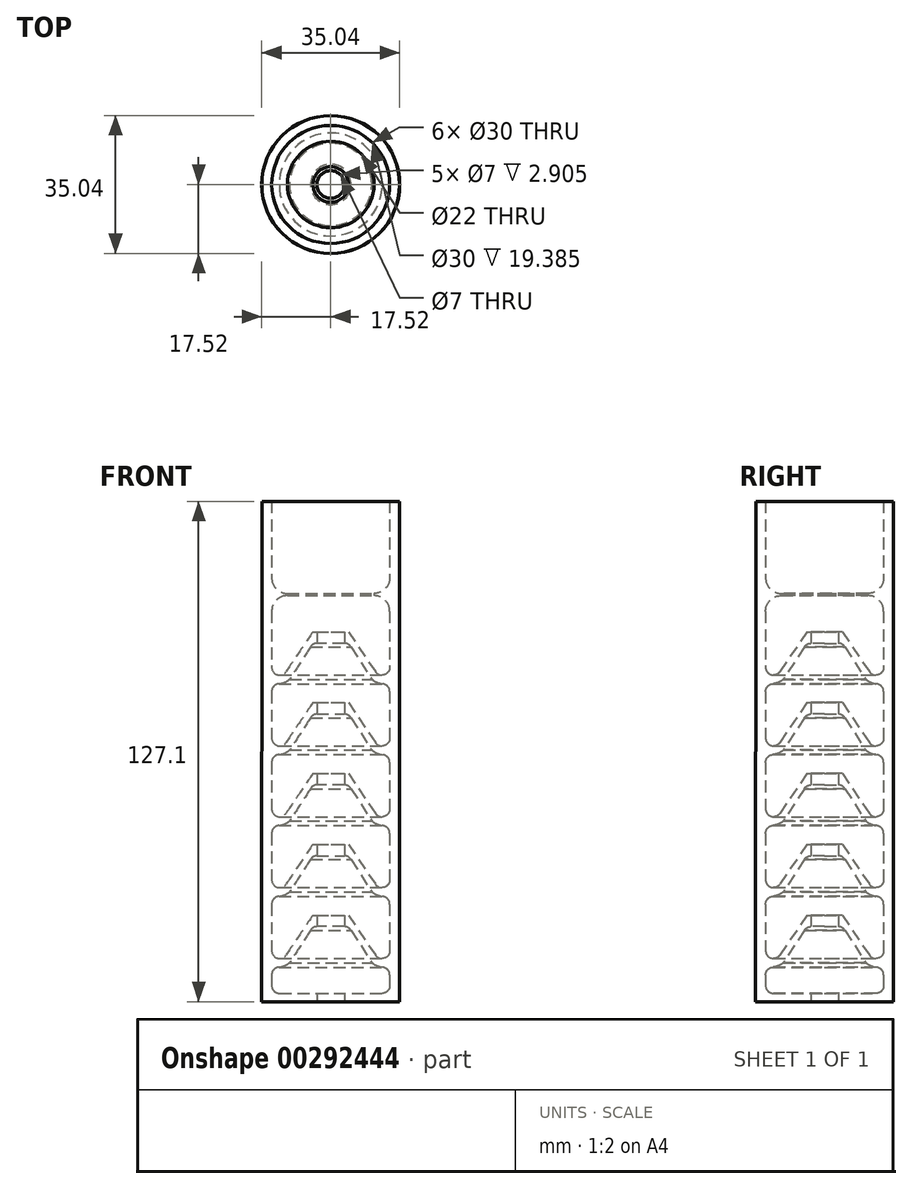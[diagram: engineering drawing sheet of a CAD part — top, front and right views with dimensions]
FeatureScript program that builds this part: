
annotation { "Feature Type Name" : "Feature", "Feature Type Description" : "" }
export const myFeature = defineFeature(function(context is Context, id is Id, definition is map)
    precondition{}
    {
        {
            var Q0;
            Q0=qCreatedBy(makeId("Front.planeOp"),FACE);
            var sketch = newSketch(context, id + "F0", { "sketchPlane" : qUnion([Q0]), "disableImprinting" : false});
            skLineSegment(sketch, "E0", {"start": v(0, 0) * mm, "end": v(0, 125) * mm, "construction": true});
            skLineSegment(sketch, "E1", {"start": v(-17.5, 0) * mm, "end": v(-17.5, 125) * mm, "construction": true});
            skLineSegment(sketch, "E2", {"start": v(-3.5, 0) * mm, "end": v(-3.5, 135) * mm, "construction": true});
            skLineSegment(sketch, "E3", {"start": v(-23.39, 125) * mm, "end": v(3.77, 125) * mm, "construction": true});
            skCircle(sketch, "E4", {"center": v(-13, 4.66) * mm, "radius": 2 * mm, "construction": true});
            skCircle(sketch, "E5", {"center": v(-13, 10.87) * mm, "radius": 2 * mm, "construction": true});
            skLineSegment(sketch, "E6", {"start": v(-4.52, 19.87) * mm, "end": v(-11.34, 9.75) * mm, "construction": true});
            skLineSegment(sketch, "E7", {"start": v(-3.57, 18.4) * mm, "end": v(-11.13, 6.77) * mm, "construction": true});
            skArc(sketch, "E8", {"start": v(-15, 4.66) * mm, "mid": v(-14.44, 6.05) * mm, "end": v(-13.08, 6.66) * mm});
            skArc(sketch, "E9", {"start": v(-15, 10.87) * mm, "mid": v(-13.58, 8.96) * mm, "end": v(-11.34, 9.75) * mm});
            skLineSegment(sketch, "E10", {"start": v(-3.5, 19.87) * mm, "end": v(-4.52, 19.87) * mm});
            skLineSegment(sketch, "E11", {"start": v(-11.34, 9.75) * mm, "end": v(-4.52, 19.87) * mm});
            skArc(sketch, "E12", {"start": v(-5.14, 16) * mm, "mid": v(-4.45, 16.7) * mm, "end": v(-3.5, 16.97) * mm});
            skLineSegment(sketch, "E13", {"start": v(-3.5, 16.97) * mm, "end": v(0, 16.97) * mm});
            skLineSegment(sketch, "E14", {"start": v(0, 16.97) * mm, "end": v(0, 19.87) * mm});
            skLineSegment(sketch, "E15", {"start": v(0, 19.87) * mm, "end": v(-3.5, 19.87) * mm});
            skLineSegment(sketch, "E16", {"start": v(-10.46, 7.8) * mm, "end": v(-5.14, 16) * mm});
            skLineSegment(sketch, "E17.direction2", {"start": v(-15, 4.66) * mm, "end": v(-15, 24.66) * mm, "construction": true});
            skCircle(sketch, "E18", {"center": v(-13, 2) * mm, "radius": 2 * mm, "construction": true});
            skArc(sketch, "E19", {"start": v(-15, 2) * mm, "mid": v(-14.41, 0.59) * mm, "end": v(-13, 0) * mm});
            skLineSegment(sketch, "E20", {"start": v(0, 0) * mm, "end": v(0, -2.1) * mm});
            skLineSegment(sketch, "E21", {"start": v(0, -2.1) * mm, "end": v(-17.52, -2.1) * mm});
            skLineSegment(sketch, "E22", {"start": v(-17.52, -2.1) * mm, "end": v(-17.5, 125) * mm});
            skLineSegment(sketch, "E23", {"start": v(-17.5, 125) * mm, "end": v(-15, 125) * mm});
            skLineSegment(sketch, "E24", {"start": v(-15, 2) * mm, "end": v(-15, 4.66) * mm});
            skArc(sketch, "E25", {"start": v(-13.08, 6.66) * mm, "mid": v(-11.7, 7.05) * mm, "end": v(-10.46, 7.8) * mm});
            skLineSegment(sketch, "E26.0.1.0", {"start": v(0, 37.87) * mm, "end": v(-3.5, 37.87) * mm});
            skArc(sketch, "E26.0.1.1", {"start": v(-5.14, 34) * mm, "mid": v(-4.45, 34.7) * mm, "end": v(-3.5, 34.97) * mm});
            skLineSegment(sketch, "E26.0.1.3", {"start": v(-4.52, 37.87) * mm, "end": v(-11.34, 27.75) * mm, "construction": true});
            skLineSegment(sketch, "E26.0.1.4", {"start": v(-3.57, 36.4) * mm, "end": v(-11.13, 24.77) * mm, "construction": true});
            skLineSegment(sketch, "E26.0.1.5", {"start": v(-3.5, 37.87) * mm, "end": v(-4.52, 37.87) * mm});
            skLineSegment(sketch, "E26.0.1.6", {"start": v(0, 34.97) * mm, "end": v(0, 37.87) * mm});
            skArc(sketch, "E26.0.1.7", {"start": v(-13.08, 24.66) * mm, "mid": v(-11.7, 25.05) * mm, "end": v(-10.46, 25.8) * mm});
            skLineSegment(sketch, "E26.0.1.8", {"start": v(-3.5, 34.97) * mm, "end": v(0, 34.97) * mm});
            skArc(sketch, "E26.0.1.9", {"start": v(-15, 22.66) * mm, "mid": v(-14.44, 24.05) * mm, "end": v(-13.08, 24.66) * mm});
            skLineSegment(sketch, "E26.0.1.10", {"start": v(-11.34, 27.75) * mm, "end": v(-4.52, 37.87) * mm});
            skLineSegment(sketch, "E26.0.1.11", {"start": v(-10.46, 25.8) * mm, "end": v(-5.14, 34) * mm});
            skArc(sketch, "E26.0.1.12", {"start": v(-15, 28.87) * mm, "mid": v(-13.58, 26.96) * mm, "end": v(-11.34, 27.75) * mm});
            skLineSegment(sketch, "E26.0.2.0", {"start": v(0, 55.87) * mm, "end": v(-3.5, 55.87) * mm});
            skArc(sketch, "E26.0.2.1", {"start": v(-5.14, 52) * mm, "mid": v(-4.45, 52.7) * mm, "end": v(-3.5, 52.97) * mm});
            skLineSegment(sketch, "E26.0.2.3", {"start": v(-4.52, 55.87) * mm, "end": v(-11.34, 45.75) * mm, "construction": true});
            skLineSegment(sketch, "E26.0.2.4", {"start": v(-3.57, 54.4) * mm, "end": v(-11.13, 42.77) * mm, "construction": true});
            skLineSegment(sketch, "E26.0.2.5", {"start": v(-3.5, 55.87) * mm, "end": v(-4.52, 55.87) * mm});
            skLineSegment(sketch, "E26.0.2.6", {"start": v(0, 52.97) * mm, "end": v(0, 55.87) * mm});
            skArc(sketch, "E26.0.2.7", {"start": v(-13.08, 42.66) * mm, "mid": v(-11.7, 43.05) * mm, "end": v(-10.46, 43.8) * mm});
            skLineSegment(sketch, "E26.0.2.8", {"start": v(-3.5, 52.97) * mm, "end": v(0, 52.97) * mm});
            skArc(sketch, "E26.0.2.9", {"start": v(-15, 40.66) * mm, "mid": v(-14.44, 42.05) * mm, "end": v(-13.08, 42.66) * mm});
            skLineSegment(sketch, "E26.0.2.10", {"start": v(-11.34, 45.75) * mm, "end": v(-4.52, 55.87) * mm});
            skLineSegment(sketch, "E26.0.2.11", {"start": v(-10.46, 43.8) * mm, "end": v(-5.14, 52) * mm});
            skArc(sketch, "E26.0.2.12", {"start": v(-15, 46.87) * mm, "mid": v(-13.58, 44.96) * mm, "end": v(-11.34, 45.75) * mm});
            skLineSegment(sketch, "E26.0.3.0", {"start": v(0, 73.87) * mm, "end": v(-3.5, 73.87) * mm});
            skArc(sketch, "E26.0.3.1", {"start": v(-5.14, 70) * mm, "mid": v(-4.45, 70.7) * mm, "end": v(-3.5, 70.97) * mm});
            skLineSegment(sketch, "E26.0.3.3", {"start": v(-4.52, 73.87) * mm, "end": v(-11.34, 63.75) * mm, "construction": true});
            skLineSegment(sketch, "E26.0.3.4", {"start": v(-3.57, 72.4) * mm, "end": v(-11.13, 60.77) * mm, "construction": true});
            skLineSegment(sketch, "E26.0.3.5", {"start": v(-3.5, 73.87) * mm, "end": v(-4.52, 73.87) * mm});
            skLineSegment(sketch, "E26.0.3.6", {"start": v(0, 70.97) * mm, "end": v(0, 73.87) * mm});
            skArc(sketch, "E26.0.3.7", {"start": v(-13.08, 60.66) * mm, "mid": v(-11.7, 61.05) * mm, "end": v(-10.46, 61.8) * mm});
            skLineSegment(sketch, "E26.0.3.8", {"start": v(-3.5, 70.97) * mm, "end": v(0, 70.97) * mm});
            skArc(sketch, "E26.0.3.9", {"start": v(-15, 58.66) * mm, "mid": v(-14.44, 60.05) * mm, "end": v(-13.08, 60.66) * mm});
            skLineSegment(sketch, "E26.0.3.10", {"start": v(-11.34, 63.75) * mm, "end": v(-4.52, 73.87) * mm});
            skLineSegment(sketch, "E26.0.3.11", {"start": v(-10.46, 61.8) * mm, "end": v(-5.14, 70) * mm});
            skArc(sketch, "E26.0.3.12", {"start": v(-15, 64.87) * mm, "mid": v(-13.58, 62.96) * mm, "end": v(-11.34, 63.75) * mm});
            skLineSegment(sketch, "E26.0.4.0", {"start": v(0, 91.87) * mm, "end": v(-3.5, 91.87) * mm});
            skArc(sketch, "E26.0.4.1", {"start": v(-5.14, 88) * mm, "mid": v(-4.45, 88.7) * mm, "end": v(-3.5, 88.97) * mm});
            skLineSegment(sketch, "E26.0.4.3", {"start": v(-4.52, 91.87) * mm, "end": v(-11.34, 81.75) * mm, "construction": true});
            skLineSegment(sketch, "E26.0.4.4", {"start": v(-3.57, 90.4) * mm, "end": v(-11.13, 78.77) * mm, "construction": true});
            skLineSegment(sketch, "E26.0.4.5", {"start": v(-3.5, 91.87) * mm, "end": v(-4.52, 91.87) * mm});
            skLineSegment(sketch, "E26.0.4.6", {"start": v(0, 88.97) * mm, "end": v(0, 91.87) * mm});
            skArc(sketch, "E26.0.4.7", {"start": v(-13.08, 78.66) * mm, "mid": v(-11.7, 79.05) * mm, "end": v(-10.46, 79.8) * mm});
            skLineSegment(sketch, "E26.0.4.8", {"start": v(-3.5, 88.97) * mm, "end": v(0, 88.97) * mm});
            skArc(sketch, "E26.0.4.9", {"start": v(-15, 76.66) * mm, "mid": v(-14.44, 78.05) * mm, "end": v(-13.08, 78.66) * mm});
            skLineSegment(sketch, "E26.0.4.10", {"start": v(-11.34, 81.75) * mm, "end": v(-4.52, 91.87) * mm});
            skLineSegment(sketch, "E26.0.4.11", {"start": v(-10.46, 79.8) * mm, "end": v(-5.14, 88) * mm});
            skArc(sketch, "E26.0.4.12", {"start": v(-15, 82.87) * mm, "mid": v(-13.58, 80.96) * mm, "end": v(-11.34, 81.75) * mm});
            skLineSegment(sketch, "E26.direction1", {"start": v(-15, 4.66) * mm, "end": v(10, 4.66) * mm, "construction": true});
            skLineSegment(sketch, "E26.direction2", {"start": v(-15, 4.66) * mm, "end": v(-15, 22.66) * mm, "construction": true});
            skLineSegment(sketch, "E27", {"start": v(-15, 28.87) * mm, "end": v(-15, 40.66) * mm});
            skLineSegment(sketch, "E28", {"start": v(-15, 46.87) * mm, "end": v(-15, 58.66) * mm});
            skLineSegment(sketch, "E29", {"start": v(-15, 64.87) * mm, "end": v(-15, 76.66) * mm});
            skLineSegment(sketch, "E30", {"start": v(-15, 82.87) * mm, "end": v(-15, 97.07) * mm});
            skLineSegment(sketch, "E31", {"start": v(0, -2.1) * mm, "end": v(0, 0) * mm});
            skLineSegment(sketch, "E32", {"start": v(0, 0) * mm, "end": v(-13, 0) * mm});
            skLineSegment(sketch, "E33", {"start": v(-15, 10.87) * mm, "end": v(-15, 22.66) * mm});
            skArc(sketch, "E34", {"start": v(-15, 97.07) * mm, "mid": v(-13.83, 99.9) * mm, "end": v(-11, 101.07) * mm});
            skArc(sketch, "E35", {"start": v(-11, 101.62) * mm, "mid": v(-13.83, 102.79) * mm, "end": v(-15, 105.62) * mm});
            skLineSegment(sketch, "E36", {"start": v(-11, 101.07) * mm, "end": v(-11, 101.62) * mm});
            skLineSegment(sketch, "E37", {"start": v(-15, 105.62) * mm, "end": v(-15, 105.62) * mm});
            skLineSegment(sketch, "E38", {"start": v(-15, 105.62) * mm, "end": v(-15, 125) * mm});
            skLineSegment(sketch, "E39", {"start": v(-15, 97.07) * mm, "end": v(-15, 97.07) * mm});
            skSolve(sketch);
        }
        {
            var Q0;
            Q0 = qSketchRegion(id + "F0", true);
            var Q1;
            Q1=sQuery(id+"F0.wireOp",EDGE,"E0");
            revolve(context, id + "F1", {"entities" : qUnion([Q0]), "axis" : qUnion([Q1]), "revolveType" : RevolveType.FULL});
        }
        {
            var Q0;
            Q0=makeQuery(id+"F1.opRevolve","SWEPT_FACE",FACE,{"disambiguationData":[OSD([sQuery(id+"F0.wireOp",EDGE,"E21")])]});
            var sketch = newSketch(context, id + "F2", { "sketchPlane" : qUnion([Q0])});
            skCircle(sketch, "E40", {"center": v(0, 0) * mm, "radius": 3.5 * mm});
            skSolve(sketch);
        }
        {
            var Q0;
            Q0 = qSketchRegion(id + "F2", true);
            extrude(context, id + "F3", {"entities" : qUnion([Q0]), "operationType" : NewBodyOperationType.REMOVE, "oppositeDirection" : true, "depth" : 125 * mm});
        }
    });
